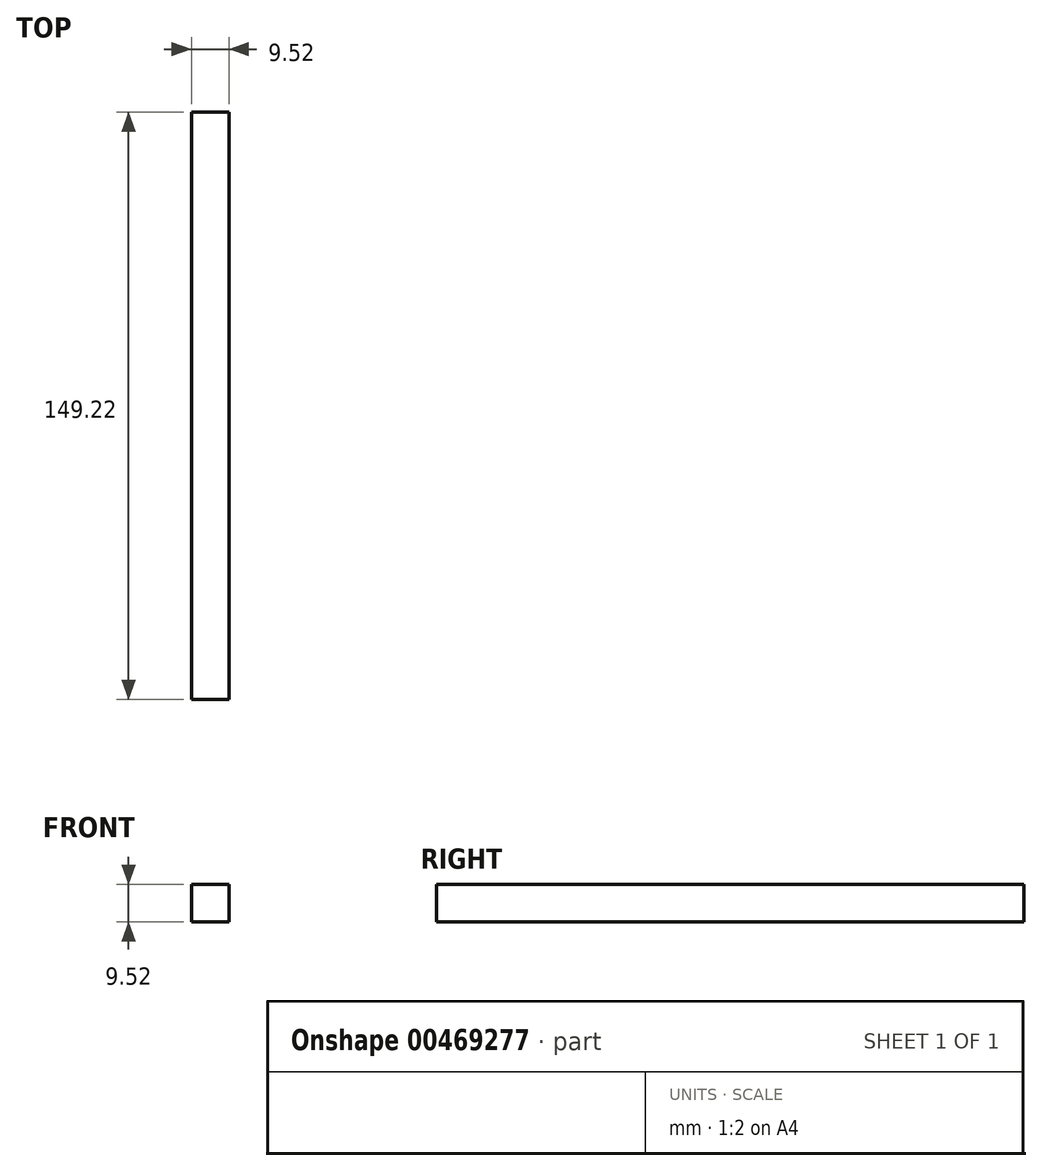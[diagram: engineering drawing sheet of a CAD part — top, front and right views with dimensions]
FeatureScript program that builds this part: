
annotation { "Feature Type Name" : "Feature", "Feature Type Description" : "" }
export const myFeature = defineFeature(function(context is Context, id is Id, definition is map)
    precondition{}
    {
        {
            var Q0;
            Q0=qCreatedBy(makeId("Front.planeOp"),FACE);
            var sketch = newSketch(context, id + "F0", { "sketchPlane" : qUnion([Q0])});
            skLineSegment(sketch, "E0.rect.bottom", {"start": v(-4.76, -4.76) * mm, "end": v(4.76, -4.76) * mm});
            skLineSegment(sketch, "E0.rect.top", {"start": v(-4.76, 4.76) * mm, "end": v(4.76, 4.76) * mm});
            skLineSegment(sketch, "E0.rect.left", {"start": v(-4.76, -4.76) * mm, "end": v(-4.76, 4.76) * mm});
            skLineSegment(sketch, "E0.rect.right", {"start": v(4.76, -4.76) * mm, "end": v(4.76, 4.76) * mm});
            skPoint(sketch, "E0.rect.middle", {"position": v(0, 0) * mm});
            skSolve(sketch);
        }
        {
            var Q0;
            Q0=makeQuery(id+"F0.imprint","IMPRINT",FACE,{"disambiguationData":[TD([[makeQuery(id+"F0.imprint","IMPRINT",EDGE,{"derivedFrom":sQuery(id+"F0.wireOp",EDGE,"E0.rect.bottom")}),1.0]])]});
            extrude(context, id + "F1", {"entities" : qUnion([Q0]), "endBound" : BoundingType.SYMMETRIC, "depth" : 149.22 * mm});
        }
    });
